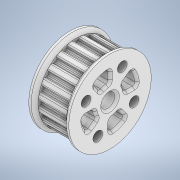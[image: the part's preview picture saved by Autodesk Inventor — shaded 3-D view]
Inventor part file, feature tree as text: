
AUTODESK INVENTOR PART (.ipt)
format: ipt  version: 2020 (Build 240168000, 168)  size: 1,275,392 bytes
history: native  units: mm
features: thicken_offset x9, sketch x9, extrude x8, projected_geometry x7, chamfer x4, pattern_circular x2, plane x1, fillet x1, hole x1, other x1
ambient origin geometry x8: Origin, YZ Plane, XZ Plane, XY Plane, X Axis, Y Axis, Z Axis, Center Point
bodies: Solid1 (feature_tree)
feature tree (43):
  extrude  "Extrusion1"  Depth=10.0mm TaperAngle=0.0deg
  plane  "Work Plane1"
  extrude  "Extrusion2"  Depth=50.0mm
  extrude  "Extrusion3"  Depth=10.0mm TaperAngle=0.0deg
  thicken_offset  "Thicken1"
  extrude  "Extrusion4"  Depth=9.0mm
  pattern_circular  "Circular Pattern1"  Count=4  [1 undecoded]
  extrude  "Extrusion5"  Depth=10.0mm TaperAngle=0.0deg
  extrude  "Extrusion6"  Depth=3.0mm TaperAngle=0.0deg
  extrude  "Extrusion7"  Depth=3.0mm TaperAngle=0.0deg
  extrude  "Extrusion8"  Depth=2.0mm
  thicken_offset  "Thicken2"
  fillet  "Fillet1"  Radius=25.0mm
  pattern_circular  "Circular Pattern2"  [2 undecoded]
  thicken_offset  "Thicken3"
  thicken_offset  "Thicken4"
  hole  "Hole1"  [1 undecoded]
  chamfer  "Chamfer2"  Distance=1.0mm
  thicken_offset  "Thicken5"
  thicken_offset  "Thicken6"
  thicken_offset  "Thicken7"
  thicken_offset  "Thicken8"
  chamfer  "Chamfer4"  Distance=1.0mm
  chamfer  "Chamfer5"  Distance=1.0mm
  thicken_offset  "Thicken9"
  chamfer  "Chamfer6"  Distance=40.0mm
  sketch  "Sketch1"  dims[d0=50.0mm d1=10.0mm d2=0.0mm]
  sketch  "Sketch2"  dims[d3=-1.0mm d4=50.0mm]
  sketch  "Sketch3"  dims[d5=10.0mm d6=0.0mm d7=10.0mm d8=0.0mm]
  projected_geometry  "Projected Loop1"
  sketch  "Sketch4"  dims[d9=9.0mm d10=9.0mm]
  projected_geometry  "Projected Loop2"
  sketch  "Sketch5"  dims[d11=11.45mm]
  projected_geometry  "Projected Loop3"
  sketch  "Sketch6"  dims[d12=4.0mm]
  projected_geometry  "Projected Loop4"
  sketch  "Sketch7"  dims[d13=10.0mm d14=0.0mm d15=40.0mm d16=62.831853mm]
  projected_geometry  "Projected Loop5"
  sketch  "Sketch8"  dims[d18=6.0mm d19=10.0mm d20=0.0mm]
  projected_geometry  "Projected Loop6"
  sketch  "Sketch9"  dims[d21=36.0mm d22=3.0mm d23=0.0mm d24=3.0mm d25=0.0mm d26=13.0mm d27=25.0mm d28=4.7mm d29=16.0mm d30=0.0mm d31=1.0mm d32=1.0mm d33=1.0mm d34=40.0mm d35=62.831853mm d40=1.0mm d41=1.0mm d42=1.0mm d43=1.0mm d44=4.15mm d45=6.0mm d46=4.0mm d47=2.0mm d48=90.0deg d49=20.0mm d50=0.0mm d51=1.0mm d52=2.0mm d53=45.0deg d54=0.5mm d55=0.7mm d56=0.5mm d57=0.7mm d61=0.5mm d62=1.0mm d63=0.5mm d64=1.0mm d65=1.5mm d66=2.0mm d67=45.0deg d68=1.5mm d69=2.0mm d70=45.0deg d71=0.025mm d72=0.025mm d73=1.0mm d74=2.0mm d75=45.0deg]
  projected_geometry  "Projected Loop7"
  other  "_ATP20XL025-A-C10_b"
note: 4 required parameter values undecoded (feature->parameter linkage not recoverable at this tier; creation-order binding heuristic only, values carry confidence <= 0.55)
